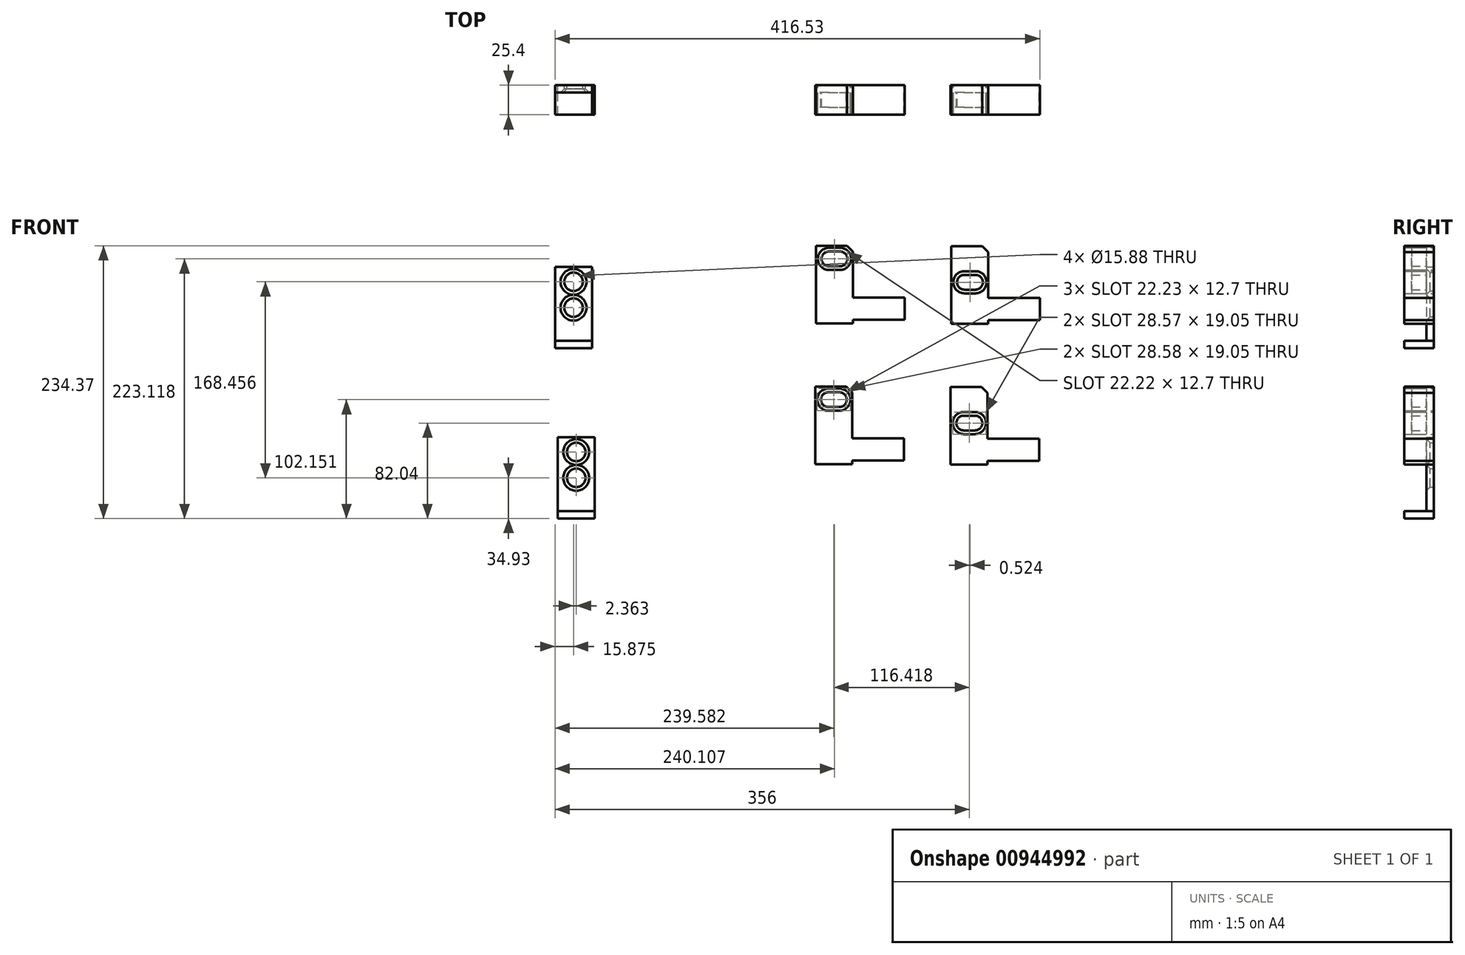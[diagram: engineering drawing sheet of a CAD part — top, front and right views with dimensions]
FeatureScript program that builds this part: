
annotation { "Feature Type Name" : "Feature", "Feature Type Description" : "" }
export const myFeature = defineFeature(function(context is Context, id is Id, definition is map)
    precondition{}
    {
        {
            var Q0;
            Q0=qCreatedBy(makeId("Front.planeOp"),FACE);
            var sketch = newSketch(context, id + "F0", { "sketchPlane" : qUnion([Q0])});
            skLineSegment(sketch, "E0.bottom", {"start": v(-94.47, 66.68) * mm, "end": v(-62.72, 66.68) * mm});
            skLineSegment(sketch, "E0.top", {"start": v(-94.47, 0) * mm, "end": v(-62.72, 0) * mm});
            skLineSegment(sketch, "E0.right", {"start": v(-94.47, 66.68) * mm, "end": v(-94.47, 0) * mm});
            skLineSegment(sketch, "E1.top", {"start": v(-62.72, 22.23) * mm, "end": v(-18.27, 22.23) * mm});
            skLineSegment(sketch, "E2.top", {"start": v(-62.72, 3.18) * mm, "end": v(-18.27, 3.18) * mm});
            skLineSegment(sketch, "E2.right", {"start": v(-18.27, 22.23) * mm, "end": v(-18.27, 3.18) * mm});
            skLineSegment(sketch, "E3", {"start": v(-62.72, 66.68) * mm, "end": v(-62.72, 22.23) * mm});
            skLineSegment(sketch, "E4.left", {"start": v(-62.72, 0) * mm, "end": v(-62.72, 3.18) * mm});
            skLineSegment(sketch, "E4.right", {"start": v(-62.72, 0) * mm, "end": v(-62.72, 3.18) * mm});
            skLineSegment(sketch, "E5", {"start": v(-83.3, 61.77) * mm, "end": v(-73.77, 61.77) * mm});
            skLineSegment(sketch, "E6", {"start": v(-83.3, 49.07) * mm, "end": v(-73.77, 49.07) * mm});
            skArc(sketch, "E7", {"start": v(-73.77, 61.77) * mm, "mid": v(-67.42, 55.42) * mm, "end": v(-73.77, 49.07) * mm});
            skArc(sketch, "E8", {"start": v(-83.3, 61.77) * mm, "mid": v(-89.65, 55.42) * mm, "end": v(-83.3, 49.07) * mm});
            skLineSegment(sketch, "E9", {"start": v(-83.3, 64.94) * mm, "end": v(-73.77, 64.94) * mm});
            skLineSegment(sketch, "E10", {"start": v(-73.77, 45.9) * mm, "end": v(-83.3, 45.9) * mm});
            skArc(sketch, "E11", {"start": v(-83.3, 64.94) * mm, "mid": v(-92.82, 55.42) * mm, "end": v(-83.3, 45.9) * mm});
            skArc(sketch, "E12", {"start": v(-73.77, 64.94) * mm, "mid": v(-64.25, 55.42) * mm, "end": v(-73.77, 45.9) * mm});
            skLineSegment(sketch, "E13.bottom", {"start": v(21.7, 66.43) * mm, "end": v(53.44, 66.43) * mm});
            skLineSegment(sketch, "E13.top", {"start": v(21.7, -0.25) * mm, "end": v(53.44, -0.25) * mm});
            skLineSegment(sketch, "E13.right", {"start": v(21.7, 66.43) * mm, "end": v(21.7, -0.25) * mm});
            skLineSegment(sketch, "E14.top", {"start": v(53.44, 21.98) * mm, "end": v(97.9, 21.98) * mm});
            skLineSegment(sketch, "E15.top", {"start": v(53.44, 2.93) * mm, "end": v(97.9, 2.93) * mm});
            skLineSegment(sketch, "E15.right", {"start": v(97.9, 21.98) * mm, "end": v(97.9, 2.93) * mm});
            skLineSegment(sketch, "E16", {"start": v(53.44, 66.43) * mm, "end": v(53.44, 21.98) * mm});
            skLineSegment(sketch, "E17.left", {"start": v(53.44, -0.25) * mm, "end": v(53.44, 2.93) * mm});
            skLineSegment(sketch, "E17.right", {"start": v(53.44, -0.25) * mm, "end": v(53.44, 2.93) * mm});
            skLineSegment(sketch, "E18", {"start": v(33.12, 41.66) * mm, "end": v(42.65, 41.66) * mm});
            skLineSegment(sketch, "E19", {"start": v(33.12, 28.96) * mm, "end": v(42.65, 28.96) * mm});
            skArc(sketch, "E20", {"start": v(42.65, 41.66) * mm, "mid": v(49, 35.3) * mm, "end": v(42.65, 28.96) * mm});
            skArc(sketch, "E21", {"start": v(33.12, 41.66) * mm, "mid": v(26.77, 35.3) * mm, "end": v(33.12, 28.96) * mm});
            skLineSegment(sketch, "E22", {"start": v(33.12, 44.83) * mm, "end": v(42.65, 44.83) * mm});
            skLineSegment(sketch, "E23", {"start": v(42.65, 25.78) * mm, "end": v(33.12, 25.78) * mm});
            skArc(sketch, "E24", {"start": v(33.12, 44.83) * mm, "mid": v(23.6, 35.3) * mm, "end": v(33.12, 25.78) * mm});
            skArc(sketch, "E25", {"start": v(42.65, 44.83) * mm, "mid": v(52.17, 35.3) * mm, "end": v(42.65, 25.78) * mm});
            skLineSegment(sketch, "E26.bottom", {"start": v(-95, -54.3) * mm, "end": v(-63.25, -54.3) * mm});
            skLineSegment(sketch, "E26.top", {"start": v(-95, -120.97) * mm, "end": v(-63.25, -120.97) * mm});
            skLineSegment(sketch, "E26.right", {"start": v(-95, -54.3) * mm, "end": v(-95, -120.97) * mm});
            skLineSegment(sketch, "E27.top", {"start": v(-63.25, -98.74) * mm, "end": v(-18.8, -98.74) * mm});
            skLineSegment(sketch, "E28.top", {"start": v(-63.25, -117.8) * mm, "end": v(-18.8, -117.8) * mm});
            skLineSegment(sketch, "E28.right", {"start": v(-18.8, -98.74) * mm, "end": v(-18.8, -117.8) * mm});
            skLineSegment(sketch, "E29", {"start": v(-63.25, -54.3) * mm, "end": v(-63.25, -98.74) * mm});
            skLineSegment(sketch, "E30.left", {"start": v(-63.25, -120.97) * mm, "end": v(-63.25, -117.8) * mm});
            skLineSegment(sketch, "E30.right", {"start": v(-63.25, -120.97) * mm, "end": v(-63.25, -117.8) * mm});
            skLineSegment(sketch, "E31", {"start": v(-83.82, -59.2) * mm, "end": v(-74.3, -59.2) * mm});
            skLineSegment(sketch, "E32", {"start": v(-83.82, -71.9) * mm, "end": v(-74.3, -71.9) * mm});
            skArc(sketch, "E33", {"start": v(-74.3, -59.2) * mm, "mid": v(-67.94, -65.55) * mm, "end": v(-74.3, -71.9) * mm});
            skArc(sketch, "E34", {"start": v(-83.82, -59.2) * mm, "mid": v(-90.17, -65.55) * mm, "end": v(-83.82, -71.9) * mm});
            skLineSegment(sketch, "E35", {"start": v(-83.82, -56.02) * mm, "end": v(-74.3, -56.02) * mm});
            skLineSegment(sketch, "E36", {"start": v(-74.3, -75.07) * mm, "end": v(-83.82, -75.07) * mm});
            skArc(sketch, "E37", {"start": v(-83.82, -56.02) * mm, "mid": v(-93.34, -65.55) * mm, "end": v(-83.82, -75.07) * mm});
            skArc(sketch, "E38", {"start": v(-74.3, -56.02) * mm, "mid": v(-64.77, -65.55) * mm, "end": v(-74.3, -75.07) * mm});
            skLineSegment(sketch, "E39.bottom", {"start": v(21.17, -54.54) * mm, "end": v(52.92, -54.54) * mm});
            skLineSegment(sketch, "E39.top", {"start": v(21.17, -121.21) * mm, "end": v(52.92, -121.21) * mm});
            skLineSegment(sketch, "E39.right", {"start": v(21.17, -54.54) * mm, "end": v(21.17, -121.21) * mm});
            skLineSegment(sketch, "E40.top", {"start": v(52.92, -98.99) * mm, "end": v(97.37, -98.99) * mm});
            skLineSegment(sketch, "E41.top", {"start": v(52.92, -118.04) * mm, "end": v(97.37, -118.04) * mm});
            skLineSegment(sketch, "E41.right", {"start": v(97.37, -98.99) * mm, "end": v(97.37, -118.04) * mm});
            skLineSegment(sketch, "E42", {"start": v(52.92, -54.54) * mm, "end": v(52.92, -98.99) * mm});
            skLineSegment(sketch, "E43.left", {"start": v(52.92, -121.21) * mm, "end": v(52.92, -118.04) * mm});
            skLineSegment(sketch, "E43.right", {"start": v(52.92, -121.21) * mm, "end": v(52.92, -118.04) * mm});
            skLineSegment(sketch, "E44", {"start": v(32.6, -79.31) * mm, "end": v(42.12, -79.31) * mm});
            skLineSegment(sketch, "E45", {"start": v(32.6, -92.01) * mm, "end": v(42.12, -92.01) * mm});
            skArc(sketch, "E46", {"start": v(42.12, -79.31) * mm, "mid": v(48.47, -85.66) * mm, "end": v(42.12, -92.01) * mm});
            skArc(sketch, "E47", {"start": v(32.6, -79.31) * mm, "mid": v(26.25, -85.66) * mm, "end": v(32.6, -92.01) * mm});
            skLineSegment(sketch, "E48", {"start": v(32.6, -76.14) * mm, "end": v(42.12, -76.14) * mm});
            skLineSegment(sketch, "E49", {"start": v(42.12, -95.19) * mm, "end": v(32.6, -95.19) * mm});
            skArc(sketch, "E50", {"start": v(32.6, -76.14) * mm, "mid": v(23.07, -85.66) * mm, "end": v(32.6, -95.19) * mm});
            skArc(sketch, "E51", {"start": v(42.12, -76.14) * mm, "mid": v(51.65, -85.66) * mm, "end": v(42.12, -95.19) * mm});
            skLineSegment(sketch, "E52.bottom", {"start": v(-318.64, 48.39) * mm, "end": v(-286.9, 48.39) * mm});
            skLineSegment(sketch, "E52.top", {"start": v(-318.64, -21.46) * mm, "end": v(-286.9, -21.46) * mm});
            skLineSegment(sketch, "E52.left", {"start": v(-318.64, 48.39) * mm, "end": v(-318.64, -21.46) * mm});
            skLineSegment(sketch, "E52.right", {"start": v(-286.9, 48.39) * mm, "end": v(-286.9, -21.46) * mm});
            skLineSegment(sketch, "E53.top", {"start": v(-318.64, -15.11) * mm, "end": v(-286.9, -15.11) * mm});
            skLineSegment(sketch, "E53.left", {"start": v(-318.64, -21.46) * mm, "end": v(-318.64, -15.11) * mm});
            skLineSegment(sketch, "E53.right", {"start": v(-286.9, -21.46) * mm, "end": v(-286.9, -15.11) * mm});
            skCircle(sketch, "E54", {"center": v(-302.77, 35.69) * mm, "radius": 7.94 * mm});
            skCircle(sketch, "E55", {"center": v(-302.77, 13.46) * mm, "radius": 7.94 * mm});
            skPoint(sketch, "E55.centerSnap0", {"position": v(-318.64, 13.46) * mm});
            skLineSegment(sketch, "E56.bottom", {"start": v(-316.28, -97.85) * mm, "end": v(-284.53, -97.85) * mm});
            skLineSegment(sketch, "E56.top", {"start": v(-316.28, -167.7) * mm, "end": v(-284.53, -167.7) * mm});
            skLineSegment(sketch, "E56.left", {"start": v(-316.28, -97.85) * mm, "end": v(-316.28, -167.7) * mm});
            skLineSegment(sketch, "E56.right", {"start": v(-284.53, -97.85) * mm, "end": v(-284.53, -167.7) * mm});
            skLineSegment(sketch, "E57.top", {"start": v(-316.28, -161.35) * mm, "end": v(-284.53, -161.35) * mm});
            skLineSegment(sketch, "E57.left", {"start": v(-316.28, -167.7) * mm, "end": v(-316.28, -161.35) * mm});
            skLineSegment(sketch, "E57.right", {"start": v(-284.53, -167.7) * mm, "end": v(-284.53, -161.35) * mm});
            skCircle(sketch, "E58", {"center": v(-300.4, -110.55) * mm, "radius": 7.94 * mm});
            skCircle(sketch, "E59", {"center": v(-300.4, -132.77) * mm, "radius": 7.94 * mm});
            skPoint(sketch, "E59.centerSnap0", {"position": v(-316.28, -132.77) * mm});
            skSolve(sketch);
        }
        {
            var Q0;
            Q0=makeQuery(id+"F0.imprint","IMPRINT",FACE,{"disambiguationData":[TD([[makeQuery(id+"F0.imprint","IMPRINT",EDGE,{"derivedFrom":sQuery(id+"F0.wireOp",EDGE,"E0.bottom")}),-1.0]])]});
            var Q1;
            Q1=makeQuery(id+"F0.imprint","IMPRINT",FACE,{"disambiguationData":[TD([[makeQuery(id+"F0.imprint","IMPRINT",EDGE,{"derivedFrom":sQuery(id+"F0.wireOp",EDGE,"E13.bottom")}),-1.0]])]});
            var Q2;
            Q2=makeQuery(id+"F0.imprint","IMPRINT",FACE,{"disambiguationData":[TD([[makeQuery(id+"F0.imprint","IMPRINT",EDGE,{"derivedFrom":sQuery(id+"F0.wireOp",EDGE,"E26.bottom")}),-1.0]])]});
            var Q3;
            Q3=makeQuery(id+"F0.imprint","IMPRINT",FACE,{"disambiguationData":[TD([[makeQuery(id+"F0.imprint","IMPRINT",EDGE,{"derivedFrom":sQuery(id+"F0.wireOp",EDGE,"E39.bottom")}),-1.0]])]});
            extrude(context, id + "F1", {"entities" : qUnion([Q0, Q1, Q2, Q3]), "depth" : 25.4 * mm, "offsetDistance" : 25.4 * mm});
        }
        {
            var Q0;
            Q0=makeQuery(id+"F0.imprint","IMPRINT",FACE,{"disambiguationData":[TD([[makeQuery(id+"F0.imprint","IMPRINT",EDGE,{"derivedFrom":sQuery(id+"F0.wireOp",EDGE,"E5")}),1.0]])]});
            var Q1;
            Q1=makeQuery(id+"F0.imprint","IMPRINT",FACE,{"disambiguationData":[TD([[makeQuery(id+"F0.imprint","IMPRINT",EDGE,{"derivedFrom":sQuery(id+"F0.wireOp",EDGE,"E18")}),1.0]])]});
            var Q2;
            Q2=makeQuery(id+"F0.imprint","IMPRINT",FACE,{"disambiguationData":[TD([[makeQuery(id+"F0.imprint","IMPRINT",EDGE,{"derivedFrom":sQuery(id+"F0.wireOp",EDGE,"E31")}),1.0]])]});
            var Q3;
            Q3=makeQuery(id+"F0.imprint","IMPRINT",FACE,{"disambiguationData":[TD([[makeQuery(id+"F0.imprint","IMPRINT",EDGE,{"derivedFrom":sQuery(id+"F0.wireOp",EDGE,"E44")}),1.0]])]});
            extrude(context, id + "F2", {"entities" : qUnion([Q0, Q1, Q2, Q3]), "depth" : 12.7 * mm, "offsetDistance" : 25.4 * mm});
        }
        {
            var Q0;
            Q0=makeQuery(id+"F2.opExtrude","SWEPT_BODY",BODY,{"disambiguationData":[OSD([sQuery(id+"F0.wireOp",EDGE,"E5"),sQuery(id+"F0.wireOp",EDGE,"E6"),sQuery(id+"F0.wireOp",EDGE,"E7"),sQuery(id+"F0.wireOp",EDGE,"E8"),sQuery(id+"F0.wireOp",EDGE,"E9"),sQuery(id+"F0.wireOp",EDGE,"E10"),sQuery(id+"F0.wireOp",EDGE,"E11"),sQuery(id+"F0.wireOp",EDGE,"E12")])]});
            var Q1;
            Q1=makeQuery(id+"F2.opExtrude","SWEPT_BODY",BODY,{"disambiguationData":[OSD([sQuery(id+"F0.wireOp",EDGE,"E18"),sQuery(id+"F0.wireOp",EDGE,"E19"),sQuery(id+"F0.wireOp",EDGE,"E20"),sQuery(id+"F0.wireOp",EDGE,"E21"),sQuery(id+"F0.wireOp",EDGE,"E22"),sQuery(id+"F0.wireOp",EDGE,"E23"),sQuery(id+"F0.wireOp",EDGE,"E24"),sQuery(id+"F0.wireOp",EDGE,"E25")])]});
            var Q2;
            Q2=makeQuery(id+"F2.opExtrude","SWEPT_BODY",BODY,{"disambiguationData":[OSD([sQuery(id+"F0.wireOp",EDGE,"E44"),sQuery(id+"F0.wireOp",EDGE,"E45"),sQuery(id+"F0.wireOp",EDGE,"E46"),sQuery(id+"F0.wireOp",EDGE,"E47"),sQuery(id+"F0.wireOp",EDGE,"E48"),sQuery(id+"F0.wireOp",EDGE,"E49"),sQuery(id+"F0.wireOp",EDGE,"E50"),sQuery(id+"F0.wireOp",EDGE,"E51")])]});
            var Q3;
            Q3=makeQuery(id+"F2.opExtrude","SWEPT_BODY",BODY,{"disambiguationData":[OSD([sQuery(id+"F0.wireOp",EDGE,"E31"),sQuery(id+"F0.wireOp",EDGE,"E32"),sQuery(id+"F0.wireOp",EDGE,"E33"),sQuery(id+"F0.wireOp",EDGE,"E34"),sQuery(id+"F0.wireOp",EDGE,"E35"),sQuery(id+"F0.wireOp",EDGE,"E36"),sQuery(id+"F0.wireOp",EDGE,"E37"),sQuery(id+"F0.wireOp",EDGE,"E38")])]});
            transform(context, id + "F3", {"entities" : qUnion([Q0, Q1, Q2, Q3]), "transformType" : TransformType.TRANSLATION_3D, "dx" : 0 * mm, "dy" : -6.35 * mm, "dz" : 0 * mm, "makeCopy" : false});
        }
        {
            var Q0;
            {var subQ2=sQuery(id+"F0.wireOp",EDGE,"E52.bottom");Q0=makeQuery(id+"F0.imprint","IMPRINT",FACE,{"disambiguationData":[TD([[makeQuery(id+"F0.imprint","IMPRINT",EDGE,{"derivedFrom":subQ2}),-1.0]])]});}
            extrude(context, id + "F4", {"entities" : qUnion([Q0]), "depth" : 6.35 * mm, "offsetDistance" : 25.4 * mm});
        }
        {
            var Q0;
            {var subQ2=sQuery(id+"F0.wireOp",EDGE,"E56.bottom");Q0=makeQuery(id+"F0.imprint","IMPRINT",FACE,{"disambiguationData":[TD([[makeQuery(id+"F0.imprint","IMPRINT",EDGE,{"derivedFrom":subQ2}),-1.0]])]});}
            extrude(context, id + "F5", {"entities" : qUnion([Q0]), "depth" : 6.35 * mm, "offsetDistance" : 25.4 * mm});
        }
        {
            var Q0;
            {var subQ0=sQuery(id+"F0.wireOp",EDGE,"E52.top");Q0=makeQuery(id+"F0.imprint","IMPRINT",FACE,{"disambiguationData":[TD([[makeQuery(id+"F0.imprint","IMPRINT",EDGE,{"derivedFrom":subQ0}),1.0]])]});}
            var Q1;
            {var subQ0=sQuery(id+"F0.wireOp",EDGE,"E56.top");Q1=makeQuery(id+"F0.imprint","IMPRINT",FACE,{"disambiguationData":[TD([[makeQuery(id+"F0.imprint","IMPRINT",EDGE,{"derivedFrom":subQ0}),1.0]])]});}
            extrude(context, id + "F6", {"entities" : qUnion([Q0, Q1]), "depth" : 25.4 * mm, "offsetDistance" : 25.4 * mm});
        }
        {
            var Q0;
            Q0=makeQuery(id+"F4.opExtrude","CAP_EDGE",EDGE,{"disambiguationData":[OSD([sQuery(id+"F0.wireOp",EDGE,"E55")])],"isStart":false});
            var Q1;
            Q1=makeQuery(id+"F4.opExtrude","CAP_EDGE",EDGE,{"disambiguationData":[OSD([sQuery(id+"F0.wireOp",EDGE,"E54")])],"isStart":false});
            var Q2;
            Q2=makeQuery(id+"F5.opExtrude","CAP_EDGE",EDGE,{"disambiguationData":[OSD([sQuery(id+"F0.wireOp",EDGE,"E58")])],"isStart":false});
            var Q3;
            Q3=makeQuery(id+"F5.opExtrude","CAP_EDGE",EDGE,{"disambiguationData":[OSD([sQuery(id+"F0.wireOp",EDGE,"E59")])],"isStart":false});
            chamfer(context, id + "F7", {"entities" : qUnion([Q0, Q1, Q2, Q3]), "width" : 3.17 * mm, "tangentPropagation" : true});
        }
        {
            var Q0;
            Q0=makeQuery(id+"F1.opExtrude","SWEPT_EDGE",EDGE,{"disambiguationData":[OSD([sQuery(id+"F0.wireOp",EDGE,"E0.bottom"),sQuery(id+"F0.wireOp",EDGE,"E3")])]});
            var Q1;
            Q1=makeQuery(id+"F1.opExtrude","SWEPT_EDGE",EDGE,{"disambiguationData":[OSD([sQuery(id+"F0.wireOp",EDGE,"E13.bottom"),sQuery(id+"F0.wireOp",EDGE,"E16")])]});
            var Q2;
            Q2=makeQuery(id+"F1.opExtrude","SWEPT_EDGE",EDGE,{"disambiguationData":[OSD([sQuery(id+"F0.wireOp",EDGE,"E39.bottom"),sQuery(id+"F0.wireOp",EDGE,"E42")])]});
            var Q3;
            Q3=makeQuery(id+"F1.opExtrude","SWEPT_EDGE",EDGE,{"disambiguationData":[OSD([sQuery(id+"F0.wireOp",EDGE,"E26.bottom"),sQuery(id+"F0.wireOp",EDGE,"E29")])]});
            chamfer(context, id + "F8", {"entities" : qUnion([Q0, Q1, Q2, Q3]), "width" : 5.08 * mm, "tangentPropagation" : true});
        }
    });
